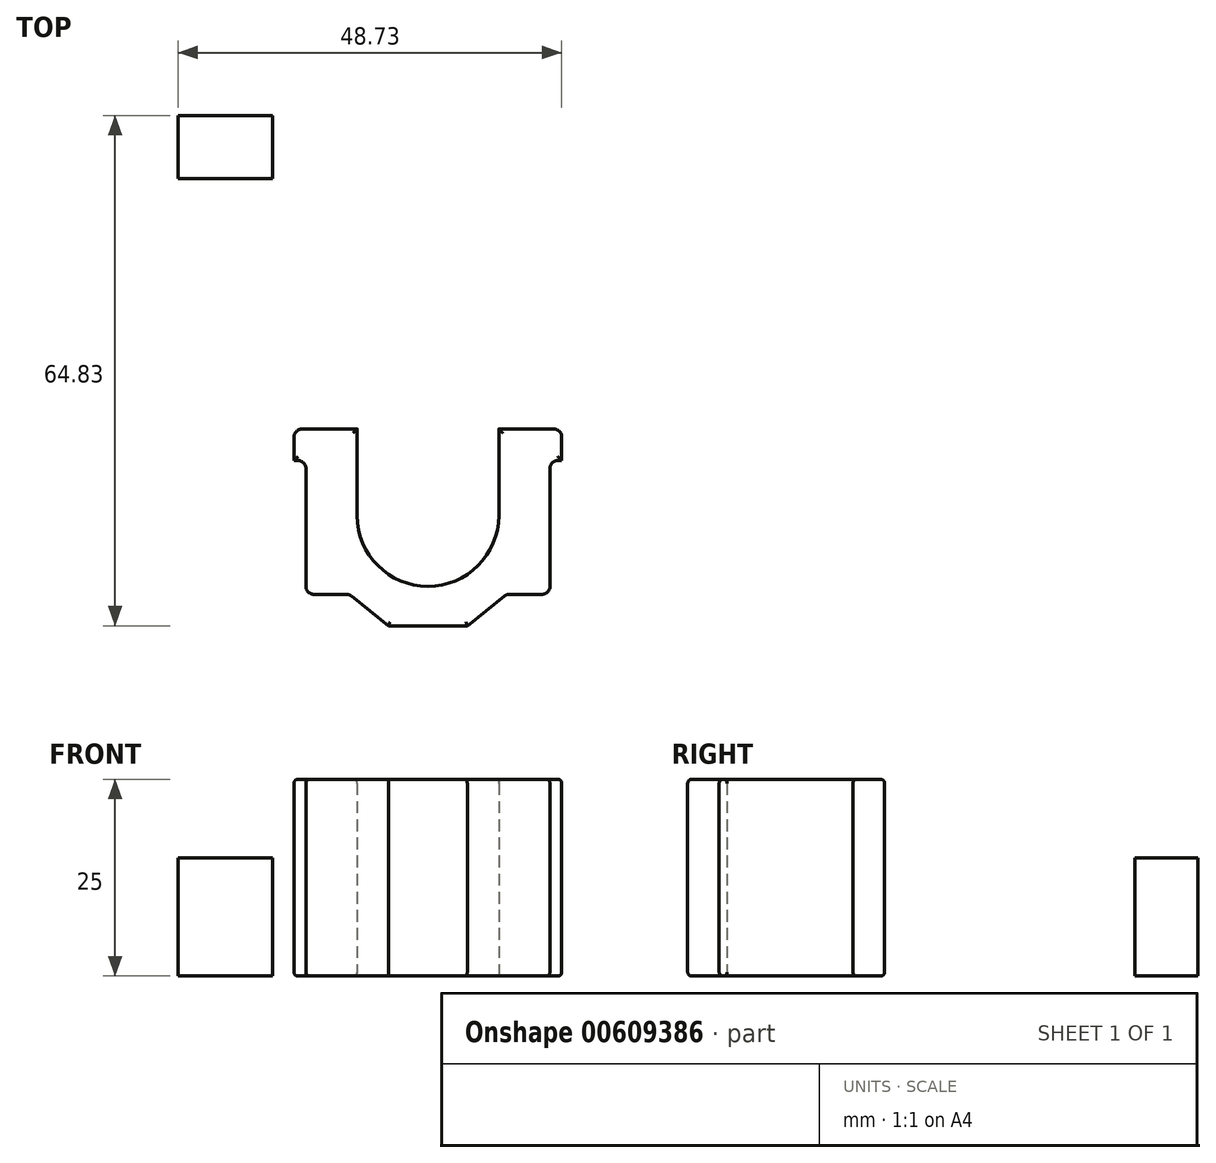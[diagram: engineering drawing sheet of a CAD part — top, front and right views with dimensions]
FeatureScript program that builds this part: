
annotation { "Feature Type Name" : "Feature", "Feature Type Description" : "" }
export const myFeature = defineFeature(function(context is Context, id is Id, definition is map)
    precondition{}
    {
        {
            var Q0;
            Q0=qCreatedBy(makeId("Top.planeOp"),FACE);
            var sketch = newSketch(context, id + "F0", { "sketchPlane" : qUnion([Q0])});
            skLineSegment(sketch, "E0.bottom", {"start": v(-48.73, 39.83) * mm, "end": v(-36.73, 39.83) * mm});
            skLineSegment(sketch, "E0.top", {"start": v(-48.73, 31.83) * mm, "end": v(-36.73, 31.83) * mm});
            skLineSegment(sketch, "E0.left", {"start": v(-48.73, 39.83) * mm, "end": v(-48.73, 31.83) * mm});
            skLineSegment(sketch, "E0.right", {"start": v(-36.73, 39.83) * mm, "end": v(-36.73, 31.83) * mm});
            skSolve(sketch);
        }
        {
            var Q0;
            Q0=makeQuery(id+"F0.imprint","IMPRINT",FACE,{"disambiguationData":[TD([[makeQuery(id+"F0.imprint","IMPRINT",EDGE,{"derivedFrom":sQuery(id+"F0.wireOp",EDGE,"E0.bottom")}),-1.0]])]});
            extrude(context, id + "F1", {"entities" : qUnion([Q0]), "depth" : 15 * mm, "offsetDistance" : 25 * mm});
        }
        {
            var Q0;
            Q0=qCreatedBy(makeId("Top.planeOp"),FACE);
            var sketch = newSketch(context, id + "F2", { "sketchPlane" : qUnion([Q0])});
            skLineSegment(sketch, "E1.bottom", {"start": v(0, 0) * mm, "end": v(-8, 0) * mm});
            skLineSegment(sketch, "E1.top", {"start": v(0, -25) * mm, "end": v(-34, -25) * mm});
            skLineSegment(sketch, "E1.left", {"start": v(0, 0) * mm, "end": v(0, -25) * mm});
            skLineSegment(sketch, "E1.right", {"start": v(-34, 0) * mm, "end": v(-34, -25) * mm});
            skArc(sketch, "E2", {"start": v(-26, -11) * mm, "mid": v(-17, -20) * mm, "end": v(-8, -11) * mm});
            skPoint(sketch, "E2.centerSnap0", {"position": v(-17, -25) * mm});
            skLineSegment(sketch, "E3", {"start": v(-26, -11) * mm, "end": v(-26, 0) * mm});
            skLineSegment(sketch, "E4", {"start": v(-8, -11) * mm, "end": v(-8, 0) * mm});
            skLineSegment(sketch, "E5.trimOffspring", {"start": v(-26, 0) * mm, "end": v(-34, 0) * mm});
            skArc(sketch, "E6", {"start": v(-8, -11) * mm, "mid": v(-17, -2) * mm, "end": v(-26, -11) * mm, "construction": true});
            skSolve(sketch);
        }
        {
            var Q0;
            Q0=makeQuery(id+"F2.imprint","IMPRINT",FACE,{"disambiguationData":[TD([[makeQuery(id+"F2.imprint","IMPRINT",EDGE,{"derivedFrom":sQuery(id+"F2.wireOp",EDGE,"E1.bottom")}),1.0]])]});
            extrude(context, id + "F3", {"entities" : qUnion([Q0]), "depth" : 25 * mm, "offsetDistance" : 25 * mm});
        }
        {
            var Q0;
            Q0=makeQuery(id+"F3.opExtrude","CAP_FACE",FACE,{"disambiguationData":[OSD([sQuery(id+"F2.wireOp",EDGE,"E1.bottom"),sQuery(id+"F2.wireOp",EDGE,"E1.top"),sQuery(id+"F2.wireOp",EDGE,"E1.left"),sQuery(id+"F2.wireOp",EDGE,"E1.right"),sQuery(id+"F2.wireOp",EDGE,"E2"),sQuery(id+"F2.wireOp",EDGE,"E3"),sQuery(id+"F2.wireOp",EDGE,"E4"),sQuery(id+"F2.wireOp",EDGE,"E5.trimOffspring")])],"isStart":false});
            var sketch = newSketch(context, id + "F4", { "sketchPlane" : qUnion([Q0])});
            skLineSegment(sketch, "E7", {"start": v(-17, -40.88) * mm, "end": v(-17, 4.13) * mm, "construction": true});
            skPoint(sketch, "E7.startSnap0", {"position": v(-17, -25) * mm});
            skLineSegment(sketch, "E8", {"start": v(-31.5, -21) * mm, "end": v(-27, -21) * mm});
            skLineSegment(sketch, "E9", {"start": v(-27, -21) * mm, "end": v(-22, -25) * mm});
            skLineSegment(sketch, "E10.MirrorCS", {"start": v(-2.5, -21) * mm, "end": v(-7, -21) * mm});
            skLineSegment(sketch, "E11.MirrorCS", {"start": v(-7, -21) * mm, "end": v(-12, -25) * mm});
            skLineSegment(sketch, "E12", {"start": v(-32.5, -20) * mm, "end": v(-32.5, -5) * mm});
            skLineSegment(sketch, "E13", {"start": v(-34, -4) * mm, "end": v(-33.5, -4) * mm});
            skPoint(sketch, "E14.orphan", {"position": v(-32.5, 0) * mm});
            skPoint(sketch, "E15.orphan", {"position": v(-34, -21) * mm});
            skLineSegment(sketch, "E16.bottom", {"start": v(-99.32, -5.66) * mm, "end": v(-92.23, -5.66) * mm});
            skLineSegment(sketch, "E16.top", {"start": v(-99.32, -17.75) * mm, "end": v(-91.23, -17.75) * mm});
            skLineSegment(sketch, "E16.left", {"start": v(-99.32, -5.66) * mm, "end": v(-99.32, -17.75) * mm});
            skLineSegment(sketch, "E16.right", {"start": v(-91.23, -6.66) * mm, "end": v(-91.23, -17.75) * mm});
            skPoint(sketch, "E17.visualSharp", {"position": v(-91.23, -5.66) * mm});
            skArc(sketch, "E17.filletArc", {"start": v(-91.23, -6.66) * mm, "mid": v(-91.52, -5.95) * mm, "end": v(-92.23, -5.66) * mm});
            skPoint(sketch, "E18.visualSharp", {"position": v(-32.5, -4) * mm});
            skArc(sketch, "E18.filletArc", {"start": v(-32.5, -5) * mm, "mid": v(-32.8, -4.3) * mm, "end": v(-33.5, -4) * mm});
            skPoint(sketch, "E19.visualSharp", {"position": v(-32.5, -21) * mm});
            skArc(sketch, "E19.filletArc", {"start": v(-32.5, -20) * mm, "mid": v(-32.2, -20.7) * mm, "end": v(-31.5, -21) * mm});
            skLineSegment(sketch, "E20.MirrorCS", {"start": v(0, -4) * mm, "end": v(-0.5, -4) * mm});
            skArc(sketch, "E21.MirrorCS", {"start": v(-1.5, -5) * mm, "mid": v(-1.2, -4.3) * mm, "end": v(-0.5, -4) * mm});
            skLineSegment(sketch, "E22.MirrorCS", {"start": v(-1.5, -20) * mm, "end": v(-1.5, -5) * mm});
            skArc(sketch, "E23.MirrorCS", {"start": v(-1.5, -20) * mm, "mid": v(-1.8, -20.7) * mm, "end": v(-2.5, -21) * mm});
            skPoint(sketch, "E24.orphan", {"position": v(0, -21) * mm});
            skSolve(sketch);
        }
        {
            var Q0;
            {var subQ0=sQuery(id+"F4.wireOp",EDGE,"E8");Q0=makeQuery(id+"F4.imprint","IMPRINT",FACE,{"disambiguationData":[TD([[makeQuery(id+"F4.imprint","IMPRINT",EDGE,{"derivedFrom":subQ0}),-1.0]])]});}
            var Q1;
            {var subQ0=sQuery(id+"F4.wireOp",EDGE,"E10.MirrorCS");Q1=makeQuery(id+"F4.imprint","IMPRINT",FACE,{"disambiguationData":[TD([[makeQuery(id+"F4.imprint","IMPRINT",EDGE,{"derivedFrom":subQ0}),1.0]])]});}
            extrude(context, id + "F5", {"entities" : qUnion([Q0, Q1]), "operationType" : NewBodyOperationType.REMOVE, "endBound" : BoundingType.THROUGH_ALL, "oppositeDirection" : true, "depth" : 25 * mm, "offsetDistance" : 25 * mm});
        }
        {
            var Q0;
            Q0=makeQuery(id+"F5.boolean.opBoolean","COPY",EDGE,{"derivedFrom":makeQuery(id+"F5.opExtrude","SWEPT_EDGE",EDGE,{"disambiguationData":[OSD([sQuery(id+"F2.wireOp",EDGE,"E1.right"),sQuery(id+"F4.wireOp",EDGE,"E13")])]})});
            var Q1;
            Q1=makeQuery(id+"F5.boolean.opBoolean","COPY",EDGE,{"derivedFrom":makeQuery(id+"F5.opExtrude","SWEPT_EDGE",EDGE,{"disambiguationData":[OSD([sQuery(id+"F2.wireOp",EDGE,"E1.left"),sQuery(id+"F4.wireOp",EDGE,"E20.MirrorCS")])]})});
            var Q2;
            Q2=makeQuery(id+"F5.boolean.opBoolean","COPY",EDGE,{"derivedFrom":makeQuery(id+"F5.opExtrude","SWEPT_EDGE",EDGE,{"disambiguationData":[OSD([sQuery(id+"F2.wireOp",EDGE,"E1.top"),sQuery(id+"F4.wireOp",EDGE,"E11.MirrorCS")])]})});
            var Q3;
            Q3=makeQuery(id+"F5.boolean.opBoolean","COPY",EDGE,{"derivedFrom":makeQuery(id+"F5.opExtrude","SWEPT_EDGE",EDGE,{"disambiguationData":[OSD([sQuery(id+"F4.wireOp",EDGE,"E10.MirrorCS"),sQuery(id+"F4.wireOp",EDGE,"E11.MirrorCS")])]})});
            var Q4;
            Q4=makeQuery(id+"F5.boolean.opBoolean","COPY",EDGE,{"derivedFrom":makeQuery(id+"F5.opExtrude","SWEPT_EDGE",EDGE,{"disambiguationData":[OSD([sQuery(id+"F4.wireOp",EDGE,"E8"),sQuery(id+"F4.wireOp",EDGE,"E9")])]})});
            var Q5;
            Q5=makeQuery(id+"F5.boolean.opBoolean","COPY",EDGE,{"derivedFrom":makeQuery(id+"F5.opExtrude","SWEPT_EDGE",EDGE,{"disambiguationData":[OSD([sQuery(id+"F2.wireOp",EDGE,"E1.top"),sQuery(id+"F4.wireOp",EDGE,"E9")])]})});
            var Q6;
            Q6=makeQuery(id+"F3.opExtrude","SWEPT_EDGE",EDGE,{"disambiguationData":[OSD([sQuery(id+"F2.wireOp",EDGE,"E1.bottom"),sQuery(id+"F2.wireOp",EDGE,"E1.left")])]});
            var Q7;
            Q7=makeQuery(id+"F3.opExtrude","SWEPT_EDGE",EDGE,{"disambiguationData":[OSD([sQuery(id+"F2.wireOp",EDGE,"E1.right"),sQuery(id+"F2.wireOp",EDGE,"E5.trimOffspring")])]});
            fillet(context, id + "F6", {"entities" : qUnion([Q0, Q1, Q2, Q3, Q4, Q5, Q6, Q7]), "radius" : 1 * mm, "tangentPropagation" : true, "allowEdgeOverflow" : false});
        }
        {
            var Q0;
            Q0=makeQuery(id+"F3.opExtrude","CAP_FACE",FACE,{"disambiguationData":[OSD([sQuery(id+"F2.wireOp",EDGE,"E1.bottom"),sQuery(id+"F2.wireOp",EDGE,"E1.top"),sQuery(id+"F2.wireOp",EDGE,"E1.left"),sQuery(id+"F2.wireOp",EDGE,"E1.right"),sQuery(id+"F2.wireOp",EDGE,"E2"),sQuery(id+"F2.wireOp",EDGE,"E3"),sQuery(id+"F2.wireOp",EDGE,"E4"),sQuery(id+"F2.wireOp",EDGE,"E5.trimOffspring")])],"isStart":false});
            var Q1;
            Q1=makeQuery(id+"F3.opExtrude","CAP_FACE",FACE,{"disambiguationData":[OSD([sQuery(id+"F2.wireOp",EDGE,"E1.bottom"),sQuery(id+"F2.wireOp",EDGE,"E1.top"),sQuery(id+"F2.wireOp",EDGE,"E1.left"),sQuery(id+"F2.wireOp",EDGE,"E1.right"),sQuery(id+"F2.wireOp",EDGE,"E2"),sQuery(id+"F2.wireOp",EDGE,"E3"),sQuery(id+"F2.wireOp",EDGE,"E4"),sQuery(id+"F2.wireOp",EDGE,"E5.trimOffspring")])],"isStart":true});
            fillet(context, id + "F7", {"entities" : qUnion([Q0, Q1]), "radius" : .5 * mm, "tangentPropagation" : true, "allowEdgeOverflow" : false});
        }
    });
